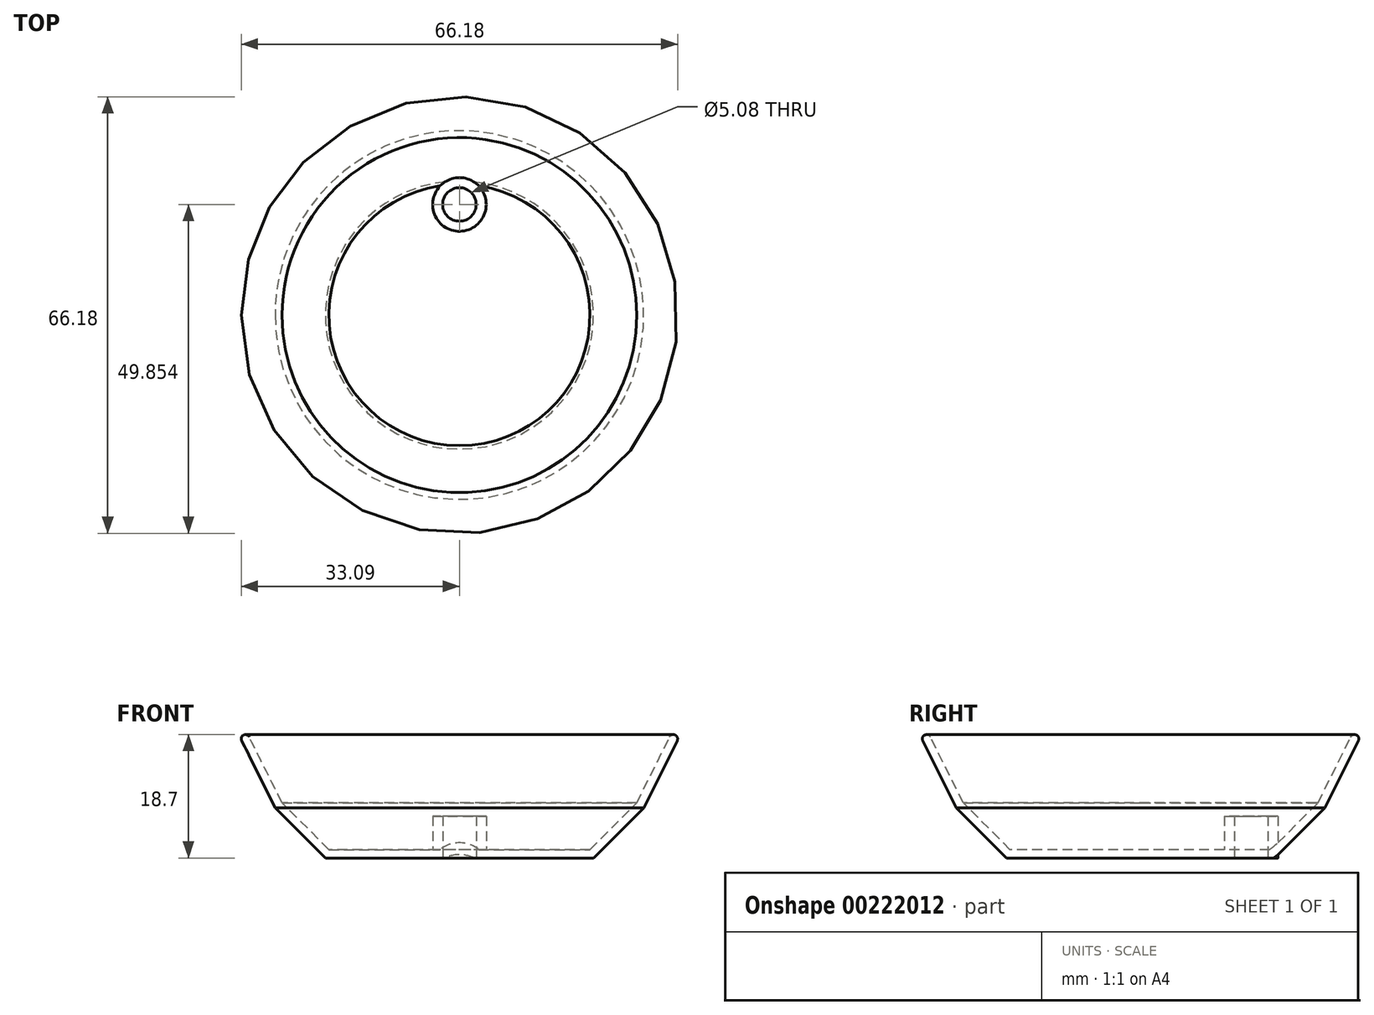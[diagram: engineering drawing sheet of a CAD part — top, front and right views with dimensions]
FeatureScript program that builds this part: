
annotation { "Feature Type Name" : "Feature", "Feature Type Description" : "" }
export const myFeature = defineFeature(function(context is Context, id is Id, definition is map)
    precondition{}
    {
        {
            var Q0;
            Q0=qCreatedBy(makeId("Front.planeOp"),FACE);
            var sketch = newSketch(context, id + "F0", { "sketchPlane" : qUnion([Q0])});
            skLineSegment(sketch, "E0", {"start": v(20.32, 0) * mm, "end": v(27.94, 7.62) * mm});
            skLineSegment(sketch, "E1", {"start": v(27.94, 7.62) * mm, "end": v(33.02, 17.78) * mm});
            skLineSegment(sketch, "E2", {"start": v(26.9, 8.37) * mm, "end": v(31.88, 18.35) * mm});
            skLineSegment(sketch, "E3", {"start": v(19.8, 1.27) * mm, "end": v(26.9, 8.37) * mm});
            skArc(sketch, "E4", {"start": v(33.02, 17.78) * mm, "mid": v(32.74, 18.63) * mm, "end": v(31.88, 18.35) * mm});
            skLineSegment(sketch, "E5", {"start": v(32.45, 18.06) * mm, "end": v(32.45, 18.7) * mm});
            skLineSegment(sketch, "E6", {"start": v(20.32, 0) * mm, "end": v(0, 0) * mm});
            skLineSegment(sketch, "E7", {"start": v(0, 0) * mm, "end": v(0, 1.27) * mm});
            skLineSegment(sketch, "E8", {"start": v(0, 1.27) * mm, "end": v(19.8, 1.27) * mm});
            skSolve(sketch);
        }
        {
            var Q0;
            Q0=makeQuery(id+"F0.imprint","IMPRINT",FACE,{"disambiguationData":[TD([[makeQuery(id+"F0.imprint","IMPRINT",EDGE,{"derivedFrom":sQuery(id+"F0.wireOp",EDGE,"E0")}),1.0]])]});
            var Q1;
            Q1=sQuery(id+"F0.wireOp",EDGE,"E7");
            revolve(context, id + "F1", {"entities" : qUnion([Q0]), "axis" : qUnion([Q1]), "revolveType" : RevolveType.FULL});
        }
        {
            var Q0;
            Q0=qCreatedBy(makeId("Top.planeOp"),FACE);
            var sketch = newSketch(context, id + "F2", { "sketchPlane" : qUnion([Q0])});
            skCircle(sketch, "E9", {"center": v(0, 16.76) * mm, "radius": 4.06 * mm});
            skCircle(sketch, "E10", {"center": v(0, 16.76) * mm, "radius": 2.54 * mm});
            skSolve(sketch);
        }
        {
            var Q0;
            Q0=qSketchRegion(id+"F2",true);
            extrude(context, id + "F3", {"entities" : qUnion([Q0]), "operationType" : NewBodyOperationType.ADD, "depth" : 6.35 * mm});
        }
        {
            var Q0;
            Q0=qCreatedBy(makeId("Top.planeOp"),FACE);
            var sketch = newSketch(context, id + "F4", { "sketchPlane" : qUnion([Q0])});
            skCircle(sketch, "E11", {"center": v(0, 16.76) * mm, "radius": 2.54 * mm});
            skSolve(sketch);
        }
        {
            var Q0;
            Q0=qSketchRegion(id+"F4",true);
            extrude(context, id + "F5", {"entities" : qUnion([Q0]), "operationType" : NewBodyOperationType.REMOVE, "depth" : 12.7 * mm, "hasSecondDirection" : true, "secondDirectionOppositeDirection" : true, "secondDirectionDepth" : 5.33 * mm});
        }
    });
